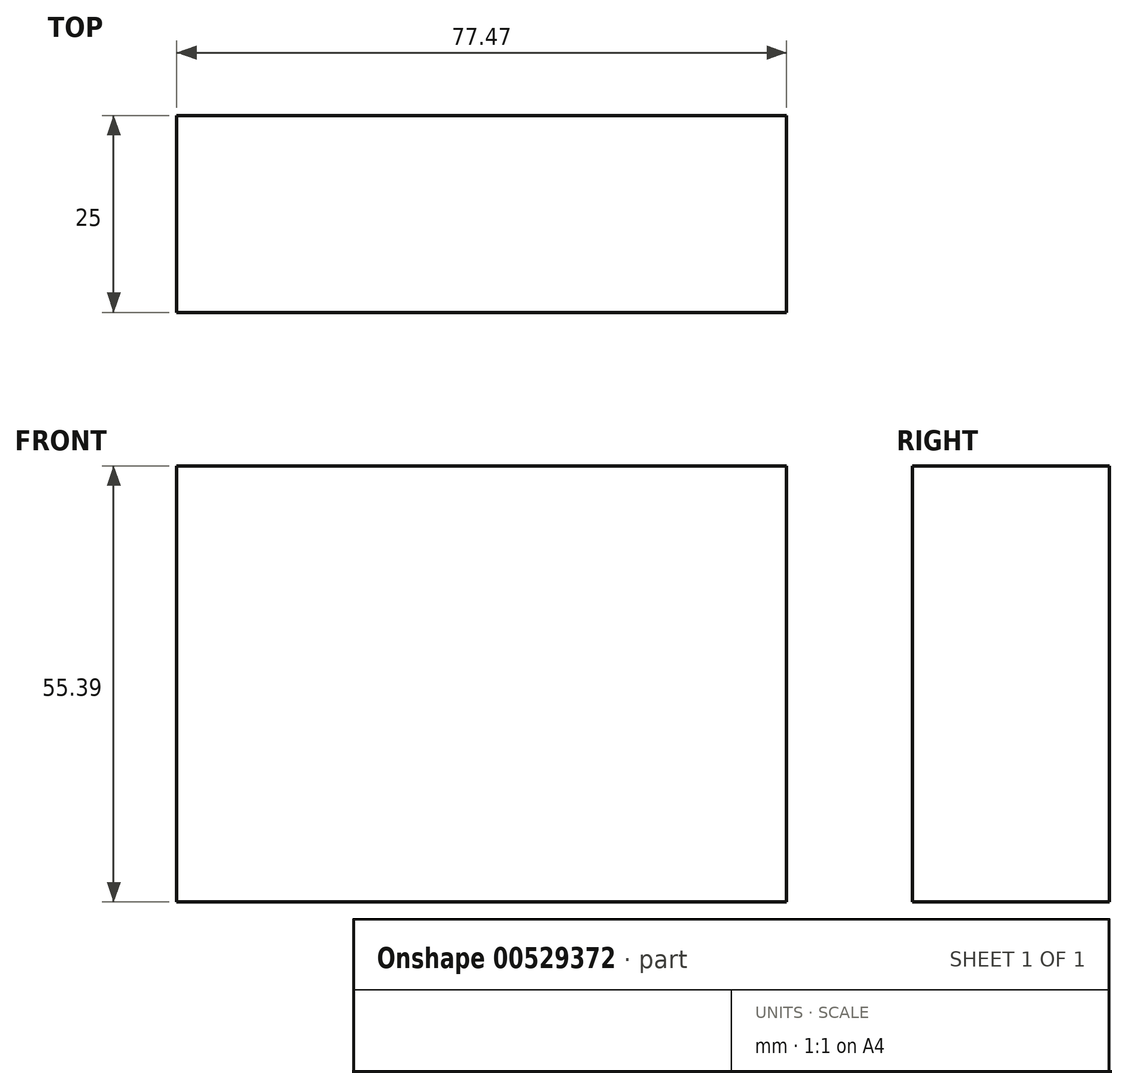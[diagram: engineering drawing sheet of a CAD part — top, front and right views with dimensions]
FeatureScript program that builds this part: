
annotation { "Feature Type Name" : "Feature", "Feature Type Description" : "" }
export const myFeature = defineFeature(function(context is Context, id is Id, definition is map)
    precondition{}
    {
        {
            var Q0;
            Q0=qCreatedBy(makeId("Front.planeOp"),FACE);
            var sketch = newSketch(context, id + "F0", { "sketchPlane" : qUnion([Q0])});
            skLineSegment(sketch, "E0.bottom", {"start": v(-32.72, 28.68) * mm, "end": v(44.75, 28.68) * mm});
            skLineSegment(sketch, "E0.top", {"start": v(-32.72, -26.7) * mm, "end": v(44.75, -26.7) * mm});
            skLineSegment(sketch, "E0.left", {"start": v(-32.72, 28.68) * mm, "end": v(-32.72, -26.7) * mm});
            skLineSegment(sketch, "E0.right", {"start": v(44.75, 28.68) * mm, "end": v(44.75, -26.7) * mm});
            skSolve(sketch);
        }
        {
            var Q0;
            Q0 = qSketchRegion(id + "F0", true);
            extrude(context, id + "F1", {"entities" : qUnion([Q0]), "depth" : 25 * mm, "offsetDistance" : 25 * mm});
        }
    });
